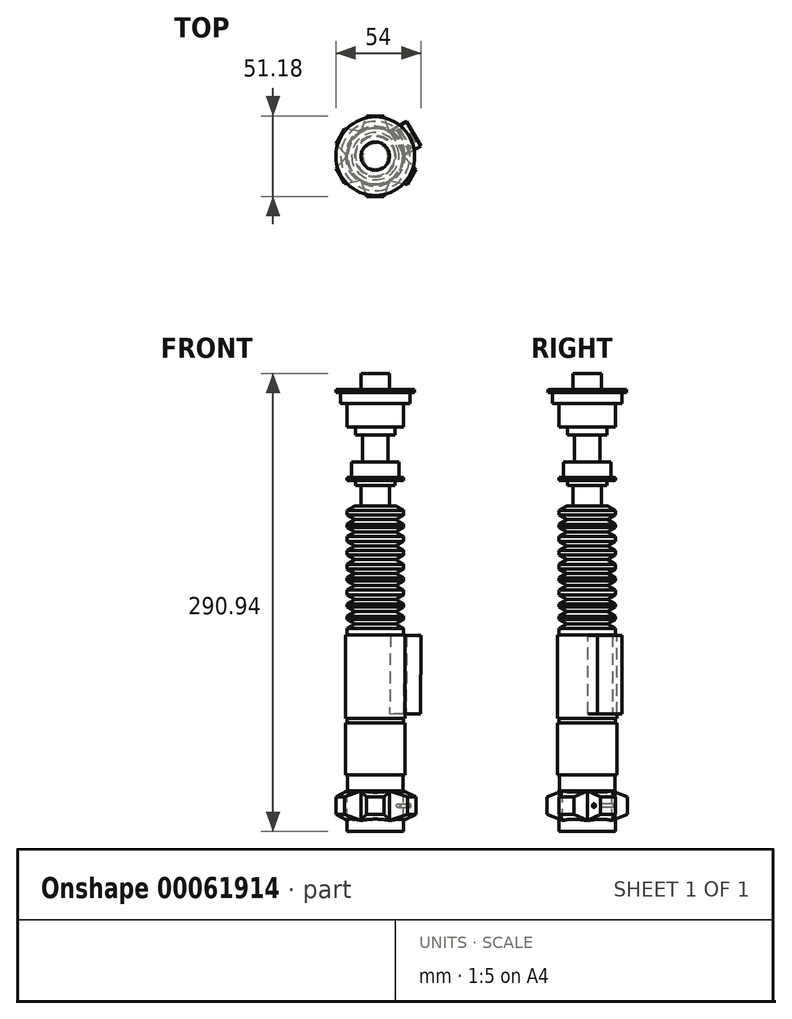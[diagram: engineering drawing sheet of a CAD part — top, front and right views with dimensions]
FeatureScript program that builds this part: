
annotation { "Feature Type Name" : "Feature", "Feature Type Description" : "" }
export const myFeature = defineFeature(function(context is Context, id is Id, definition is map)
    precondition{}
    {
        {
            var Q0;
            Q0=qCreatedBy(makeId("Front.planeOp"),FACE);
            var sketch = newSketch(context, id + "F0", { "sketchPlane" : qUnion([Q0])});
            skLineSegment(sketch, "E0.right", {"start": v(18, 0) * mm, "end": v(18, -10) * mm});
            skLineSegment(sketch, "E1", {"start": v(9, 0) * mm, "end": v(9, -95.13) * mm, "construction": true});
            skPoint(sketch, "E1.endSnap0", {"position": v(9, -10) * mm});
            skLineSegment(sketch, "E2.bottom", {"start": v(9, -10) * mm, "end": v(34, -10) * mm});
            skLineSegment(sketch, "E2.top", {"start": v(9, -12) * mm, "end": v(34, -12) * mm});
            skLineSegment(sketch, "E2.left", {"start": v(9, -10) * mm, "end": v(9, -12) * mm});
            skLineSegment(sketch, "E2.right", {"start": v(34, -10) * mm, "end": v(34, -12) * mm});
            skLineSegment(sketch, "E3.bottom", {"start": v(9, -12) * mm, "end": v(31, -12) * mm});
            skLineSegment(sketch, "E3.top", {"start": v(9, -19) * mm, "end": v(31, -19) * mm});
            skLineSegment(sketch, "E3.left", {"start": v(9, -12) * mm, "end": v(9, -19) * mm});
            skLineSegment(sketch, "E3.right", {"start": v(31, -12) * mm, "end": v(31, -19) * mm});
            skLineSegment(sketch, "E4.bottom", {"start": v(9, -19) * mm, "end": v(27, -19) * mm});
            skLineSegment(sketch, "E4.top", {"start": v(9, -34) * mm, "end": v(27, -34) * mm});
            skLineSegment(sketch, "E4.left", {"start": v(9, -19) * mm, "end": v(9, -34) * mm});
            skLineSegment(sketch, "E4.right", {"start": v(27, -19) * mm, "end": v(27, -34) * mm});
            skLineSegment(sketch, "E5.bottom", {"start": v(9, -34) * mm, "end": v(21.5, -34) * mm});
            skLineSegment(sketch, "E5.top", {"start": v(9, -39) * mm, "end": v(21.5, -39) * mm});
            skLineSegment(sketch, "E5.left", {"start": v(9, -34) * mm, "end": v(9, -39) * mm});
            skLineSegment(sketch, "E5.right", {"start": v(21.5, -34) * mm, "end": v(21.5, -39) * mm});
            skLineSegment(sketch, "E6.bottom", {"start": v(9, -39) * mm, "end": v(17, -39) * mm});
            skLineSegment(sketch, "E6.top", {"start": v(9, -56) * mm, "end": v(17, -56) * mm});
            skLineSegment(sketch, "E6.left", {"start": v(9, -39) * mm, "end": v(9, -56) * mm});
            skLineSegment(sketch, "E6.right", {"start": v(17, -39) * mm, "end": v(17, -56) * mm});
            skLineSegment(sketch, "E7.bottom", {"start": v(9, -56) * mm, "end": v(24, -56) * mm});
            skLineSegment(sketch, "E7.top", {"start": v(9, -66) * mm, "end": v(24, -66) * mm});
            skLineSegment(sketch, "E7.left", {"start": v(9, -56) * mm, "end": v(9, -66) * mm});
            skLineSegment(sketch, "E7.right", {"start": v(24, -56) * mm, "end": v(24, -66) * mm});
            skLineSegment(sketch, "E8.bottom", {"start": v(9, -66) * mm, "end": v(27, -66) * mm});
            skLineSegment(sketch, "E8.top", {"start": v(9, -68) * mm, "end": v(27, -68) * mm});
            skLineSegment(sketch, "E8.left", {"start": v(9, -66) * mm, "end": v(9, -68) * mm});
            skLineSegment(sketch, "E8.right", {"start": v(27, -66) * mm, "end": v(27, -68) * mm});
            skLineSegment(sketch, "E9.bottom", {"start": v(9, -68) * mm, "end": v(21.5, -68) * mm});
            skLineSegment(sketch, "E9.top", {"start": v(9, -71) * mm, "end": v(21.5, -71) * mm});
            skLineSegment(sketch, "E9.left", {"start": v(9, -68) * mm, "end": v(9, -71) * mm});
            skLineSegment(sketch, "E9.right", {"start": v(21.5, -68) * mm, "end": v(21.5, -71) * mm});
            skLineSegment(sketch, "E10.bottom", {"start": v(9, -71) * mm, "end": v(18, -71) * mm});
            skLineSegment(sketch, "E10.top", {"start": v(9, -84) * mm, "end": v(18, -84) * mm});
            skLineSegment(sketch, "E10.left", {"start": v(9, -71) * mm, "end": v(9, -84) * mm});
            skLineSegment(sketch, "E10.right", {"start": v(18, -71) * mm, "end": v(18, -84) * mm});
            skLineSegment(sketch, "E11", {"start": v(9, -84) * mm, "end": v(21.98, -84) * mm});
            skLineSegment(sketch, "E12.0", {"start": v(9, -86.9) * mm, "end": v(27, -86.9) * mm});
            skLineSegment(sketch, "E13", {"start": v(27, -86.9) * mm, "end": v(21.98, -84) * mm});
            skLineSegment(sketch, "E14.0", {"start": v(9, -89.9) * mm, "end": v(27, -89.9) * mm});
            skLineSegment(sketch, "E15", {"start": v(27, -86.9) * mm, "end": v(27, -89.9) * mm});
            skLineSegment(sketch, "E16", {"start": v(27, -89.9) * mm, "end": v(21.98, -92.8) * mm});
            skLineSegment(sketch, "E17.0", {"start": v(9, -92.8) * mm, "end": v(21.98, -92.8) * mm});
            skLineSegment(sketch, "E18.MirrorCS", {"start": v(27, -95.7) * mm, "end": v(21.98, -92.8) * mm});
            skLineSegment(sketch, "E19", {"start": v(27, -95.7) * mm, "end": v(9, -95.7) * mm});
            skLineSegment(sketch, "E20.0", {"start": v(27, -97.7) * mm, "end": v(9, -97.7) * mm});
            skLineSegment(sketch, "E21", {"start": v(27, -95.7) * mm, "end": v(27, -97.7) * mm});
            skLineSegment(sketch, "E22", {"start": v(27, -97.7) * mm, "end": v(21.98, -100.6) * mm});
            skLineSegment(sketch, "E23.0", {"start": v(21.98, -100.6) * mm, "end": v(9, -100.6) * mm});
            skLineSegment(sketch, "E24", {"start": v(21.98, -100.6) * mm, "end": v(27, -103.5) * mm});
            skLineSegment(sketch, "E25", {"start": v(27, -103.5) * mm, "end": v(9, -103.5) * mm});
            skLineSegment(sketch, "E26.0", {"start": v(27, -106.5) * mm, "end": v(9, -106.5) * mm});
            skLineSegment(sketch, "E27", {"start": v(27, -103.5) * mm, "end": v(27, -106.5) * mm});
            skLineSegment(sketch, "E28.MirrorCS", {"start": v(21.98, -109.4) * mm, "end": v(27, -106.5) * mm});
            skLineSegment(sketch, "E29.MirrorCS", {"start": v(21.98, -109.4) * mm, "end": v(9, -109.4) * mm});
            skLineSegment(sketch, "E30.MirrorCS", {"start": v(27, -112.3) * mm, "end": v(21.98, -109.4) * mm});
            skLineSegment(sketch, "E31.MirrorCS", {"start": v(27, -112.3) * mm, "end": v(9, -112.3) * mm});
            skLineSegment(sketch, "E32.MirrorCS", {"start": v(27, -115.3) * mm, "end": v(9, -115.3) * mm});
            skLineSegment(sketch, "E33.MirrorCS", {"start": v(21.98, -118.2) * mm, "end": v(27, -115.3) * mm});
            skLineSegment(sketch, "E34.MirrorCS", {"start": v(27, -121.1) * mm, "end": v(21.98, -118.2) * mm});
            skLineSegment(sketch, "E35.MirrorCS", {"start": v(21.98, -118.2) * mm, "end": v(9, -118.2) * mm});
            skLineSegment(sketch, "E36.MirrorCS", {"start": v(27, -121.1) * mm, "end": v(9, -121.1) * mm});
            skLineSegment(sketch, "E37.MirrorCS", {"start": v(27, -124.1) * mm, "end": v(9, -124.1) * mm});
            skLineSegment(sketch, "E38.MirrorCS", {"start": v(27, -124.1) * mm, "end": v(21.98, -127) * mm});
            skLineSegment(sketch, "E39.MirrorCS", {"start": v(21.98, -127) * mm, "end": v(9, -127) * mm});
            skLineSegment(sketch, "E40.MirrorCS", {"start": v(21.98, -127) * mm, "end": v(27, -129.9) * mm});
            skLineSegment(sketch, "E41.MirrorCS", {"start": v(27, -129.9) * mm, "end": v(9, -129.9) * mm});
            skLineSegment(sketch, "E42.MirrorCS", {"start": v(27, -129.74) * mm, "end": v(21.98, -126.84) * mm});
            skLineSegment(sketch, "E43.MirrorCS", {"start": v(27, -131.74) * mm, "end": v(9, -131.74) * mm});
            skLineSegment(sketch, "E44.MirrorCS", {"start": v(27, -131.74) * mm, "end": v(21.98, -134.64) * mm});
            skLineSegment(sketch, "E45.MirrorCS", {"start": v(9, -134.64) * mm, "end": v(21.98, -134.64) * mm});
            skLineSegment(sketch, "E46.MirrorCS", {"start": v(9, -137.54) * mm, "end": v(27, -137.54) * mm});
            skLineSegment(sketch, "E47.MirrorCS", {"start": v(9, -140.54) * mm, "end": v(27, -140.54) * mm});
            skLineSegment(sketch, "E48.MirrorCS", {"start": v(27, -140.54) * mm, "end": v(21.98, -143.44) * mm});
            skLineSegment(sketch, "E49", {"start": v(21.98, -134.64) * mm, "end": v(27, -137.54) * mm});
            skLineSegment(sketch, "E50", {"start": v(27, -140.54) * mm, "end": v(27, -137.54) * mm});
            skLineSegment(sketch, "E51", {"start": v(21.98, -143.44) * mm, "end": v(9, -143.44) * mm});
            skLineSegment(sketch, "E52.MirrorCS", {"start": v(27, -146.34) * mm, "end": v(21.98, -143.44) * mm});
            skLineSegment(sketch, "E53.MirrorCS", {"start": v(9, -146.34) * mm, "end": v(27, -146.34) * mm});
            skLineSegment(sketch, "E54", {"start": v(27, -131.74) * mm, "end": v(27, -129.74) * mm});
            skLineSegment(sketch, "E55", {"start": v(27, -124.1) * mm, "end": v(27, -121.1) * mm});
            skLineSegment(sketch, "E56.0", {"start": v(9, -148.34) * mm, "end": v(27, -148.34) * mm});
            skLineSegment(sketch, "E57", {"start": v(27, -148.34) * mm, "end": v(27, -146.34) * mm});
            skLineSegment(sketch, "E58.MirrorCS", {"start": v(27, -148.34) * mm, "end": v(21.98, -151.24) * mm});
            skLineSegment(sketch, "E59.MirrorCS", {"start": v(21.98, -151.24) * mm, "end": v(9, -151.24) * mm});
            skLineSegment(sketch, "E60.MirrorCS", {"start": v(27, -154.14) * mm, "end": v(21.98, -151.24) * mm});
            skLineSegment(sketch, "E61.MirrorCS", {"start": v(9, -154.14) * mm, "end": v(27, -154.14) * mm});
            skLineSegment(sketch, "E62.MirrorCS", {"start": v(9, -156.14) * mm, "end": v(27, -156.14) * mm});
            skLineSegment(sketch, "E63.MirrorCS", {"start": v(27, -154.14) * mm, "end": v(27, -156.14) * mm});
            skLineSegment(sketch, "E64.MirrorCS", {"start": v(27, -156.14) * mm, "end": v(21.98, -159.04) * mm});
            skLineSegment(sketch, "E65.MirrorCS", {"start": v(21.98, -159.04) * mm, "end": v(9, -159.04) * mm});
            skLineSegment(sketch, "E66.MirrorCS", {"start": v(27, -161.94) * mm, "end": v(21.98, -159.04) * mm});
            skLineSegment(sketch, "E67.MirrorCS", {"start": v(9, -161.94) * mm, "end": v(27, -161.94) * mm});
            skLineSegment(sketch, "E68", {"start": v(27, -161.94) * mm, "end": v(27, -165.94) * mm});
            skLineSegment(sketch, "E69", {"start": v(9, -165.94) * mm, "end": v(27, -165.94) * mm});
            skLineSegment(sketch, "E70", {"start": v(27, -112.3) * mm, "end": v(27, -115.3) * mm});
            skLineSegment(sketch, "E71", {"start": v(9, 0) * mm, "end": v(9, -165.94) * mm});
            skLineSegment(sketch, "E72", {"start": v(9, 0) * mm, "end": v(18, 0) * mm});
            skSolve(sketch);
        }
        {
            var Q0;
            {var subQ0=sQuery(id+"F0.wireOp",EDGE,"E39.MirrorCS");var subQ1=makeQuery(id+"F0.imprint","IMPRINT",EDGE,{"derivedFrom":subQ0});var subQ2=sQuery(id+"F0.wireOp",EDGE,"E40.MirrorCS");var subQ3=makeQuery(id+"F0.imprint","IMPRINT",EDGE,{"derivedFrom":subQ2});var subQ4=sQuery(id+"F0.wireOp",EDGE,"E41.MirrorCS");var subQ5=makeQuery(id+"F0.imprint","IMPRINT",EDGE,{"derivedFrom":subQ4});var subQ14=sQuery(id+"F0.wireOp",EDGE,"E37.MirrorCS");var subQ15=makeQuery(id+"F0.imprint","IMPRINT",EDGE,{"derivedFrom":subQ14});var subQ17=sQuery(id+"F0.wireOp",EDGE,"E65.MirrorCS");var subQ18=makeQuery(id+"F0.imprint","IMPRINT",EDGE,{"derivedFrom":subQ17});var subQ20=sQuery(id+"F0.wireOp",EDGE,"E67.MirrorCS");var subQ22=makeQuery(id+"F0.imprint","IMPRINT",EDGE,{"derivedFrom":subQ20});var subQ23=sQuery(id+"F0.wireOp",EDGE,"E62.MirrorCS");var subQ24=makeQuery(id+"F0.imprint","IMPRINT",EDGE,{"derivedFrom":subQ23});var subQ26=sQuery(id+"F0.wireOp",EDGE,"E61.MirrorCS");var subQ27=makeQuery(id+"F0.imprint","IMPRINT",EDGE,{"derivedFrom":subQ26});var subQ29=sQuery(id+"F0.wireOp",EDGE,"E59.MirrorCS");var subQ30=makeQuery(id+"F0.imprint","IMPRINT",EDGE,{"derivedFrom":subQ29});var subQ32=sQuery(id+"F0.wireOp",EDGE,"E56.0");var subQ33=makeQuery(id+"F0.imprint","IMPRINT",EDGE,{"derivedFrom":subQ32});var subQ35=sQuery(id+"F0.wireOp",EDGE,"E53.MirrorCS");var subQ36=makeQuery(id+"F0.imprint","IMPRINT",EDGE,{"derivedFrom":subQ35});var subQ38=sQuery(id+"F0.wireOp",EDGE,"E51");var subQ39=makeQuery(id+"F0.imprint","IMPRINT",EDGE,{"derivedFrom":subQ38});var subQ41=sQuery(id+"F0.wireOp",EDGE,"E47.MirrorCS");var subQ42=makeQuery(id+"F0.imprint","IMPRINT",EDGE,{"derivedFrom":subQ41});var subQ44=sQuery(id+"F0.wireOp",EDGE,"E46.MirrorCS");var subQ45=makeQuery(id+"F0.imprint","IMPRINT",EDGE,{"derivedFrom":subQ44});var subQ47=sQuery(id+"F0.wireOp",EDGE,"E45.MirrorCS");var subQ48=makeQuery(id+"F0.imprint","IMPRINT",EDGE,{"derivedFrom":subQ47});var subQ50=sQuery(id+"F0.wireOp",EDGE,"E43.MirrorCS");var subQ51=makeQuery(id+"F0.imprint","IMPRINT",EDGE,{"derivedFrom":subQ50});var subQ57=sQuery(id+"F0.wireOp",EDGE,"E36.MirrorCS");var subQ58=makeQuery(id+"F0.imprint","IMPRINT",EDGE,{"derivedFrom":subQ57});var subQ63=sQuery(id+"F0.wireOp",EDGE,"E32.MirrorCS");var subQ64=makeQuery(id+"F0.imprint","IMPRINT",EDGE,{"derivedFrom":subQ63});var subQ66=sQuery(id+"F0.wireOp",EDGE,"E31.MirrorCS");var subQ67=makeQuery(id+"F0.imprint","IMPRINT",EDGE,{"derivedFrom":subQ66});var subQ69=sQuery(id+"F0.wireOp",EDGE,"E29.MirrorCS");var subQ70=makeQuery(id+"F0.imprint","IMPRINT",EDGE,{"derivedFrom":subQ69});var subQ72=sQuery(id+"F0.wireOp",EDGE,"E26.0");var subQ73=makeQuery(id+"F0.imprint","IMPRINT",EDGE,{"derivedFrom":subQ72});var subQ75=sQuery(id+"F0.wireOp",EDGE,"E25");var subQ76=makeQuery(id+"F0.imprint","IMPRINT",EDGE,{"derivedFrom":subQ75});var subQ78=sQuery(id+"F0.wireOp",EDGE,"E23.0");var subQ79=makeQuery(id+"F0.imprint","IMPRINT",EDGE,{"derivedFrom":subQ78});var subQ81=sQuery(id+"F0.wireOp",EDGE,"E20.0");var subQ82=makeQuery(id+"F0.imprint","IMPRINT",EDGE,{"derivedFrom":subQ81});var subQ84=sQuery(id+"F0.wireOp",EDGE,"E19");var subQ85=makeQuery(id+"F0.imprint","IMPRINT",EDGE,{"derivedFrom":subQ84});var subQ87=sQuery(id+"F0.wireOp",EDGE,"E17.0");var subQ88=makeQuery(id+"F0.imprint","IMPRINT",EDGE,{"derivedFrom":subQ87});var subQ90=sQuery(id+"F0.wireOp",EDGE,"E14.0");var subQ91=makeQuery(id+"F0.imprint","IMPRINT",EDGE,{"derivedFrom":subQ90});var subQ93=sQuery(id+"F0.wireOp",EDGE,"E12.0");var subQ94=makeQuery(id+"F0.imprint","IMPRINT",EDGE,{"derivedFrom":subQ93});var subQ96=sQuery(id+"F0.wireOp",EDGE,"E10.top");var subQ97=makeQuery(id+"F0.imprint","IMPRINT",EDGE,{"derivedFrom":subQ96});var subQ99=sQuery(id+"F0.wireOp",EDGE,"E9.left");var subQ110=makeQuery(id+"F0.imprint","IMPRINT",EDGE,{"derivedFrom":sQuery(id+"F0.wireOp",EDGE,"E7.top")});var subQ111=makeQuery(id+"F0.imprint","IMPRINT",EDGE,{"derivedFrom":sQuery(id+"F0.wireOp",EDGE,"E6.top")});var subQ113=sQuery(id+"F0.wireOp",EDGE,"E5.left");var subQ119=sQuery(id+"F0.wireOp",EDGE,"E4.left");var subQ124=sQuery(id+"F0.wireOp",EDGE,"E3.left");var subQ129=sQuery(id+"F0.wireOp",EDGE,"E2.left");var subQ135=sQuery(id+"F0.wireOp",EDGE,"E0.right");Q0=qUnion([makeQuery(id+"F0.imprint","IMPRINT",FACE,{"disambiguationData":[TD([[makeQuery(id+"F0.imprint","IMPRINT",EDGE,{"derivedFrom":subQ135}),-1.0]])]}),makeQuery(id+"F0.imprint","IMPRINT",FACE,{"disambiguationData":[TD([[subQ22,-1.0]])]}),makeQuery(id+"F0.imprint","IMPRINT",FACE,{"disambiguationData":[TD([[makeQuery(id+"F0.imprint","IMPRINT",EDGE,{"derivedFrom":subQ129}),1.0]])]}),makeQuery(id+"F0.imprint","IMPRINT",FACE,{"disambiguationData":[TD([[makeQuery(id+"F0.imprint","IMPRINT",EDGE,{"derivedFrom":subQ124}),1.0]])]}),makeQuery(id+"F0.imprint","IMPRINT",FACE,{"disambiguationData":[TD([[makeQuery(id+"F0.imprint","IMPRINT",EDGE,{"derivedFrom":subQ119}),1.0]])]}),makeQuery(id+"F0.imprint","IMPRINT",FACE,{"disambiguationData":[TD([[makeQuery(id+"F0.imprint","IMPRINT",EDGE,{"derivedFrom":subQ113}),1.0]])]}),makeQuery(id+"F0.imprint","IMPRINT",FACE,{"disambiguationData":[TD([[subQ111,1.0]])]}),makeQuery(id+"F0.imprint","IMPRINT",FACE,{"disambiguationData":[TD([[subQ111,-1.0]])]}),makeQuery(id+"F0.imprint","IMPRINT",FACE,{"disambiguationData":[TD([[subQ110,-1.0]])]}),makeQuery(id+"F0.imprint","IMPRINT",FACE,{"disambiguationData":[TD([[makeQuery(id+"F0.imprint","IMPRINT",EDGE,{"derivedFrom":subQ99}),1.0]])]}),makeQuery(id+"F0.imprint","IMPRINT",FACE,{"disambiguationData":[TD([[subQ97,1.0]])]}),makeQuery(id+"F0.imprint","IMPRINT",FACE,{"disambiguationData":[TD([[subQ97,-1.0]])]}),makeQuery(id+"F0.imprint","IMPRINT",FACE,{"disambiguationData":[TD([[subQ94,-1.0]])]}),makeQuery(id+"F0.imprint","IMPRINT",FACE,{"disambiguationData":[TD([[subQ91,-1.0]])]}),makeQuery(id+"F0.imprint","IMPRINT",FACE,{"disambiguationData":[TD([[subQ88,-1.0]])]}),makeQuery(id+"F0.imprint","IMPRINT",FACE,{"disambiguationData":[TD([[subQ85,1.0]])]}),makeQuery(id+"F0.imprint","IMPRINT",FACE,{"disambiguationData":[TD([[subQ82,1.0]])]}),makeQuery(id+"F0.imprint","IMPRINT",FACE,{"disambiguationData":[TD([[subQ79,1.0]])]}),makeQuery(id+"F0.imprint","IMPRINT",FACE,{"disambiguationData":[TD([[subQ76,1.0]])]}),makeQuery(id+"F0.imprint","IMPRINT",FACE,{"disambiguationData":[TD([[subQ73,1.0]])]}),makeQuery(id+"F0.imprint","IMPRINT",FACE,{"disambiguationData":[TD([[subQ70,1.0]])]}),makeQuery(id+"F0.imprint","IMPRINT",FACE,{"disambiguationData":[TD([[subQ67,1.0]])]}),makeQuery(id+"F0.imprint","IMPRINT",FACE,{"disambiguationData":[TD([[subQ64,1.0]])]}),makeQuery(id+"F0.imprint","IMPRINT",FACE,{"disambiguationData":[TD([[makeQuery(id+"F0.imprint","IMPRINT",EDGE,{"derivedFrom":sQuery(id+"F0.wireOp",EDGE,"E34.MirrorCS")}),1.0]])]}),makeQuery(id+"F0.imprint","IMPRINT",FACE,{"disambiguationData":[TD([[subQ58,1.0]])]}),makeQuery(id+"F0.imprint","IMPRINT",FACE,{"disambiguationData":[TD([[subQ3,1.0]])]}),makeQuery(id+"F0.imprint","IMPRINT",FACE,{"disambiguationData":[TD([[subQ5,1.0]])]}),makeQuery(id+"F0.imprint","IMPRINT",FACE,{"disambiguationData":[TD([[subQ51,1.0]])]}),makeQuery(id+"F0.imprint","IMPRINT",FACE,{"disambiguationData":[TD([[subQ48,-1.0]])]}),makeQuery(id+"F0.imprint","IMPRINT",FACE,{"disambiguationData":[TD([[subQ45,-1.0]])]}),makeQuery(id+"F0.imprint","IMPRINT",FACE,{"disambiguationData":[TD([[subQ42,-1.0]])]}),makeQuery(id+"F0.imprint","IMPRINT",FACE,{"disambiguationData":[TD([[subQ39,1.0]])]}),makeQuery(id+"F0.imprint","IMPRINT",FACE,{"disambiguationData":[TD([[subQ36,-1.0]])]}),makeQuery(id+"F0.imprint","IMPRINT",FACE,{"disambiguationData":[TD([[subQ33,-1.0]])]}),makeQuery(id+"F0.imprint","IMPRINT",FACE,{"disambiguationData":[TD([[subQ30,1.0]])]}),makeQuery(id+"F0.imprint","IMPRINT",FACE,{"disambiguationData":[TD([[subQ27,-1.0]])]}),makeQuery(id+"F0.imprint","IMPRINT",FACE,{"disambiguationData":[TD([[subQ24,-1.0]])]}),makeQuery(id+"F0.imprint","IMPRINT",FACE,{"disambiguationData":[TD([[subQ18,1.0]])]}),makeQuery(id+"F0.imprint","IMPRINT",FACE,{"disambiguationData":[TD([[subQ15,1.0]])]}),makeQuery(id+"F0.imprint","IMPRINT",FACE,{"disambiguationData":[TD([[subQ1,1.0]])]})]);}
            var Q1;
            Q1=sQuery(id+"F0.wireOp",EDGE,"E71");
            revolve(context, id + "F1", {"entities" : qUnion([Q0]), "axis" : qUnion([Q1]), "revolveType" : RevolveType.FULL});
        }
        {
            var Q0;
            Q0=qCreatedBy(makeId("Front.planeOp"),FACE);
            var sketch = newSketch(context, id + "F2", { "sketchPlane" : qUnion([Q0])});
            skLineSegment(sketch, "E73.0", {"start": v(-9, -165.94) * mm, "end": v(27, -165.94) * mm});
            skLineSegment(sketch, "E74", {"start": v(9, -165.94) * mm, "end": v(9, -218.94) * mm});
            skLineSegment(sketch, "E75", {"start": v(9, -165.94) * mm, "end": v(28, -165.94) * mm});
            skLineSegment(sketch, "E76", {"start": v(28, -165.94) * mm, "end": v(28, -218.94) * mm});
            skLineSegment(sketch, "E77", {"start": v(28, -218.94) * mm, "end": v(9, -218.94) * mm});
            skLineSegment(sketch, "E78", {"start": v(9, -218.94) * mm, "end": v(9, -221.94) * mm});
            skLineSegment(sketch, "E79", {"start": v(9, -221.94) * mm, "end": v(27, -221.94) * mm});
            skLineSegment(sketch, "E80", {"start": v(27, -221.94) * mm, "end": v(27, -218.94) * mm});
            skLineSegment(sketch, "E81", {"start": v(9, -221.94) * mm, "end": v(9, -254.94) * mm});
            skLineSegment(sketch, "E82", {"start": v(9, -221.94) * mm, "end": v(28, -221.94) * mm});
            skLineSegment(sketch, "E83", {"start": v(28, -221.94) * mm, "end": v(28, -254.94) * mm});
            skLineSegment(sketch, "E84", {"start": v(28, -254.94) * mm, "end": v(9, -254.94) * mm});
            skLineSegment(sketch, "E85", {"start": v(9, -254.94) * mm, "end": v(9, -264.94) * mm});
            skLineSegment(sketch, "E86", {"start": v(9, -264.94) * mm, "end": v(26.5, -264.94) * mm});
            skLineSegment(sketch, "E87", {"start": v(26.5, -264.94) * mm, "end": v(26.5, -254.94) * mm});
            skSolve(sketch);
        }
        {
            var Q0;
            Q0 = qSketchRegion(id + "F2", true);
            var Q1;
            Q1=sQuery(id+"F2.wireOp",EDGE,"E74");
            revolve(context, id + "F3", {"operationType" : NewBodyOperationType.ADD, "entities" : qUnion([Q0]), "axis" : qUnion([Q1]), "revolveType" : RevolveType.FULL});
        }
        {
            var Q0;
            Q0=qCreatedBy(makeId("Front.planeOp"),FACE);
            var sketch = newSketch(context, id + "F4", { "sketchPlane" : qUnion([Q0])});
            skLineSegment(sketch, "E88.0", {"start": v(-8.5, -264.94) * mm, "end": v(26.5, -264.94) * mm});
            skLineSegment(sketch, "E89", {"start": v(9, -264.94) * mm, "end": v(9, -283.94) * mm});
            skLineSegment(sketch, "E90", {"start": v(9, -283.94) * mm, "end": v(27, -283.94) * mm});
            skLineSegment(sketch, "E91", {"start": v(27, -283.94) * mm, "end": v(27, -264.94) * mm});
            skLineSegment(sketch, "E92", {"start": v(27, -264.94) * mm, "end": v(9, -264.94) * mm});
            skLineSegment(sketch, "E93", {"start": v(9, -283.94) * mm, "end": v(9, -290.94) * mm});
            skLineSegment(sketch, "E94", {"start": v(9, -290.94) * mm, "end": v(27, -290.94) * mm});
            skLineSegment(sketch, "E95", {"start": v(27, -290.94) * mm, "end": v(27, -283.94) * mm});
            skSolve(sketch);
        }
        {
            var Q0;
            {var subQ0=sQuery(id+"F4.wireOp",EDGE,"E89");Q0=makeQuery(id+"F4.imprint","IMPRINT",FACE,{"disambiguationData":[TD([[makeQuery(id+"F4.imprint","IMPRINT",EDGE,{"derivedFrom":subQ0}),1.0]])]});}
            var Q1;
            Q1=sQuery(id+"F4.wireOp",EDGE,"E89");
            revolve(context, id + "F5", {"operationType" : NewBodyOperationType.ADD, "entities" : qUnion([Q0]), "axis" : qUnion([Q1]), "revolveType" : RevolveType.FULL});
        }
        {
            var Q0;
            Q0=makeQuery(id+"F5.opRevolve","SWEPT_FACE",FACE,{"disambiguationData":[OSD([sQuery(id+"F4.wireOp",EDGE,"E90")])]});
            var sketch = newSketch(context, id + "F6", { "sketchPlane" : qUnion([Q0])});
            skCircle(sketch, "E96.0", {"center": v(9, 0) * mm, "radius": 18 * mm, "construction": true});
            skLineSegment(sketch, "E97.0", {"start": v(0, -15.59) * mm, "end": v(-9, 0) * mm, "construction": true});
            skLineSegment(sketch, "E97.1", {"start": v(-9, 0) * mm, "end": v(0, 15.59) * mm, "construction": true});
            skLineSegment(sketch, "E97.2", {"start": v(0, 15.59) * mm, "end": v(18, 15.59) * mm, "construction": true});
            skLineSegment(sketch, "E97.3", {"start": v(18, 15.59) * mm, "end": v(27, 0) * mm, "construction": true});
            skLineSegment(sketch, "E97.4", {"start": v(27, 0) * mm, "end": v(18, -15.59) * mm, "construction": true});
            skLineSegment(sketch, "E97.5", {"start": v(18, -15.59) * mm, "end": v(0, -15.59) * mm, "construction": true});
            skSolve(sketch);
        }
        {
            var Q0;
            Q0=makeQuery(id+"F6.imprint","IMPRINT",FACE,{"disambiguationData":[TD([[makeQuery(id+"F6.imprint","IMPRINT",EDGE,{"derivedFrom":makeQuery(id+"F5.opRevolve","SWEPT_EDGE",EDGE,{"disambiguationData":[OSD([sQuery(id+"F4.wireOp",EDGE,"E90"),sQuery(id+"F4.wireOp",EDGE,"E91"),sQuery(id+"F4.wireOp",EDGE,"E95")])]})}),-1.0]])]});
            cPlane(context, id + "F7", {"entities" : qUnion([Q0]), "cplaneType" : CPlaneType.OFFSET, "offset" : 10 * mm, "width" : 150 * mm, "height" : 150 * mm});
        }
        {
            var Q0;
            Q0=qCreatedBy(id+"F7.planeOp",FACE);
            var sketch = newSketch(context, id + "F8", { "sketchPlane" : qUnion([Q0])});
            skLineSegment(sketch, "E98.0", {"start": v(18, 15.59) * mm, "end": v(27, 0) * mm, "construction": true});
            skLineSegment(sketch, "E98.1", {"start": v(27, 0) * mm, "end": v(18, -15.59) * mm, "construction": true});
            skLineSegment(sketch, "E98.2", {"start": v(18, -15.59) * mm, "end": v(0, -15.59) * mm, "construction": true});
            skLineSegment(sketch, "E98.3", {"start": v(0, -15.59) * mm, "end": v(-9, 0) * mm, "construction": true});
            skLineSegment(sketch, "E98.4", {"start": v(-9, 0) * mm, "end": v(0, 15.59) * mm, "construction": true});
            skLineSegment(sketch, "E98.5", {"start": v(0, 15.59) * mm, "end": v(18, 15.59) * mm, "construction": true});
            skSolve(sketch);
        }
        {
            var Q0;
            Q0=sQuery(id+"F6.wireOp",VERTEX,"E97.3.end");
            var Q1;
            Q1=sQuery(id+"F8.wireOp",VERTEX,"E98.1.start");
            var Q2;
            Q2=sQuery(id+"F6.wireOp",VERTEX,"E97.5.start");
            cPlane(context, id + "F9", {"entities" : qUnion([Q0, Q1, Q2]), "cplaneType" : CPlaneType.THREE_POINT, "offset" : 150 * mm, "width" : 150 * mm, "height" : 150 * mm});
        }
        {
            var Q0;
            Q0=qCreatedBy(id+"F9.planeOp",FACE);
            var sketch = newSketch(context, id + "F10", { "sketchPlane" : qUnion([Q0])});
            skLineSegment(sketch, "E99.0", {"start": v(13.5, -283.94) * mm, "end": v(-4.5, -283.94) * mm, "construction": true});
            skLineSegment(sketch, "E99.1", {"start": v(-13.5, -264.94) * mm, "end": v(22.5, -264.94) * mm, "construction": true});
            skLineSegment(sketch, "E100", {"start": v(13.5, -283.94) * mm, "end": v(-4.5, -283.94) * mm});
            skLineSegment(sketch, "E101", {"start": v(-4.5, -283.94) * mm, "end": v(-4.5, -264.94) * mm});
            skLineSegment(sketch, "E102", {"start": v(-4.5, -264.94) * mm, "end": v(13.5, -264.94) * mm, "construction": true});
            skLineSegment(sketch, "E103", {"start": v(13.5, -264.94) * mm, "end": v(13.5, -283.94) * mm});
            skLineSegment(sketch, "E104", {"start": v(13.5, -264.94) * mm, "end": v(-4.5, -264.94) * mm});
            skSolve(sketch);
        }
        {
            var Q0;
            Q0=qCreatedBy(id+"F9.planeOp",FACE);
            cPlane(context, id + "F11", {"entities" : qUnion([Q0]), "cplaneType" : CPlaneType.OFFSET, "offset" : 11 * mm, "oppositeDirection" : true, "width" : 150 * mm, "height" : 150 * mm});
        }
        {
            var Q0;
            Q0=qCreatedBy(id+"F11.planeOp",FACE);
            var sketch = newSketch(context, id + "F12", { "sketchPlane" : qUnion([Q0])});
            skLineSegment(sketch, "E105.0", {"start": v(13.5, -264.94) * mm, "end": v(13.5, -283.94) * mm, "construction": true});
            skLineSegment(sketch, "E105.1", {"start": v(13.5, -264.94) * mm, "end": v(-4.5, -264.94) * mm, "construction": true});
            skLineSegment(sketch, "E105.2", {"start": v(-4.5, -283.94) * mm, "end": v(-4.5, -264.94) * mm, "construction": true});
            skLineSegment(sketch, "E105.3", {"start": v(13.5, -283.94) * mm, "end": v(-4.5, -283.94) * mm, "construction": true});
            skLineSegment(sketch, "E106", {"start": v(4.5, -264.94) * mm, "end": v(4.5, -283.94) * mm, "construction": true});
            skLineSegment(sketch, "E107", {"start": v(13.5, -274.44) * mm, "end": v(-4.5, -274.44) * mm, "construction": true});
            skLineSegment(sketch, "E108", {"start": v(4.5, -268.94) * mm, "end": v(-1, -268.94) * mm});
            skLineSegment(sketch, "E109", {"start": v(-1, -268.94) * mm, "end": v(-1, -279.94) * mm});
            skLineSegment(sketch, "E110", {"start": v(-1, -279.94) * mm, "end": v(10, -279.94) * mm});
            skLineSegment(sketch, "E111", {"start": v(10, -279.94) * mm, "end": v(10, -268.94) * mm});
            skLineSegment(sketch, "E112", {"start": v(10, -268.94) * mm, "end": v(4.5, -268.94) * mm});
            skSolve(sketch);
        }
        {
            var Q1;
            Q1 = qSketchRegion(id + "F10", true);
            var Q2;
            Q2 = qSketchRegion(id + "F12", true);
            loft(context, id + "F13", {"operationType" : NewBodyOperationType.ADD, "sheetProfilesArray" : [{ "sheetProfileEntities" : qUnion([Q1]) }, { "sheetProfileEntities" : qUnion([Q2]) }]});
        }
        {
            var Q0;
            Q0=sQuery(id+"F8.wireOp",VERTEX,"E98.0.start");
            var Q1;
            Q1=sQuery(id+"F8.wireOp",VERTEX,"E98.1.start");
            var Q2;
            Q2=sQuery(id+"F6.wireOp",VERTEX,"E97.3.start");
            cPlane(context, id + "F14", {"entities" : qUnion([Q0, Q1, Q2]), "cplaneType" : CPlaneType.THREE_POINT, "offset" : 150 * mm, "width" : 150 * mm, "height" : 150 * mm});
        }
        {
            var Q0;
            Q0=qCreatedBy(id+"F14.planeOp",FACE);
            var sketch = newSketch(context, id + "F15", { "sketchPlane" : qUnion([Q0])});
            skLineSegment(sketch, "E113.0", {"start": v(4.5, -283.94) * mm, "end": v(-13.5, -283.94) * mm, "construction": true});
            skLineSegment(sketch, "E114.0", {"start": v(-22.5, -264.94) * mm, "end": v(13.5, -264.94) * mm, "construction": true});
            skLineSegment(sketch, "E115.bottom", {"start": v(4.5, -283.94) * mm, "end": v(-13.6, -283.94) * mm});
            skLineSegment(sketch, "E115.top", {"start": v(4.5, -264.94) * mm, "end": v(-13.6, -264.94) * mm});
            skLineSegment(sketch, "E115.left", {"start": v(4.5, -283.94) * mm, "end": v(4.5, -264.94) * mm});
            skLineSegment(sketch, "E115.right", {"start": v(-13.6, -283.94) * mm, "end": v(-13.6, -264.94) * mm});
            skSolve(sketch);
        }
        {
            var Q0;
            Q0=qCreatedBy(id+"F14.planeOp",FACE);
            cPlane(context, id + "F16", {"entities" : qUnion([Q0]), "cplaneType" : CPlaneType.OFFSET, "offset" : 11 * mm, "oppositeDirection" : true, "width" : 150 * mm, "height" : 150 * mm});
        }
        {
            var Q0;
            Q0=qCreatedBy(id+"F16.planeOp",FACE);
            var sketch = newSketch(context, id + "F17", { "sketchPlane" : qUnion([Q0])});
            skLineSegment(sketch, "E116.0", {"start": v(4.5, -283.94) * mm, "end": v(4.5, -264.94) * mm, "construction": true});
            skLineSegment(sketch, "E116.1", {"start": v(4.5, -283.94) * mm, "end": v(-13.6, -283.94) * mm, "construction": true});
            skLineSegment(sketch, "E116.2", {"start": v(-13.6, -283.94) * mm, "end": v(-13.6, -264.94) * mm, "construction": true});
            skLineSegment(sketch, "E116.3", {"start": v(4.5, -264.94) * mm, "end": v(-13.6, -264.94) * mm, "construction": true});
            skLineSegment(sketch, "E117", {"start": v(-4.55, -264.94) * mm, "end": v(-4.55, -283.94) * mm, "construction": true});
            skLineSegment(sketch, "E118", {"start": v(4.5, -274.44) * mm, "end": v(-13.6, -274.44) * mm, "construction": true});
            skLineSegment(sketch, "E119", {"start": v(-4.55, -268.94) * mm, "end": v(-10.05, -268.94) * mm});
            skLineSegment(sketch, "E120", {"start": v(-10.05, -268.94) * mm, "end": v(-10.05, -279.94) * mm});
            skLineSegment(sketch, "E121", {"start": v(-10.05, -279.94) * mm, "end": v(0.95, -279.94) * mm});
            skLineSegment(sketch, "E122", {"start": v(0.95, -279.94) * mm, "end": v(0.95, -268.94) * mm});
            skLineSegment(sketch, "E123", {"start": v(0.95, -268.94) * mm, "end": v(-4.55, -268.94) * mm});
            skSolve(sketch);
        }
        {
            var Q1;
            Q1 = qSketchRegion(id + "F15", true);
            var Q2;
            Q2 = qSketchRegion(id + "F17", true);
            loft(context, id + "F18", {"operationType" : NewBodyOperationType.ADD, "sheetProfilesArray" : [{ "sheetProfileEntities" : qUnion([Q1]) }, { "sheetProfileEntities" : qUnion([Q2]) }]});
        }
        {
            var Q0;
            Q0=sQuery(id+"F8.wireOp",VERTEX,"E98.0.start");
            var Q1;
            Q1=sQuery(id+"F8.wireOp",VERTEX,"E98.5.start");
            var Q2;
            Q2=sQuery(id+"F6.wireOp",VERTEX,"E97.3.start");
            cPlane(context, id + "F19", {"entities" : qUnion([Q0, Q1, Q2]), "cplaneType" : CPlaneType.THREE_POINT, "offset" : 150 * mm, "width" : 150 * mm, "height" : 150 * mm});
        }
        {
            var Q0;
            Q0=qCreatedBy(id+"F19.planeOp",FACE);
            var sketch = newSketch(context, id + "F20", { "sketchPlane" : qUnion([Q0])});
            skLineSegment(sketch, "E124.0", {"start": v(18, -283.94) * mm, "end": v(0, -283.94) * mm, "construction": true});
            skLineSegment(sketch, "E124.1", {"start": v(-9, -264.94) * mm, "end": v(18, -264.94) * mm, "construction": true});
            skLineSegment(sketch, "E125.bottom", {"start": v(0, -283.94) * mm, "end": v(18, -283.94) * mm});
            skLineSegment(sketch, "E125.top", {"start": v(0, -264.94) * mm, "end": v(18, -264.94) * mm});
            skLineSegment(sketch, "E125.left", {"start": v(0, -283.94) * mm, "end": v(0, -264.94) * mm});
            skLineSegment(sketch, "E125.right", {"start": v(18, -283.94) * mm, "end": v(18, -264.94) * mm});
            skSolve(sketch);
        }
        {
            var Q0;
            Q0=qCreatedBy(id+"F19.planeOp",FACE);
            cPlane(context, id + "F21", {"entities" : qUnion([Q0]), "cplaneType" : CPlaneType.OFFSET, "offset" : 10 * mm, "width" : 150 * mm, "height" : 150 * mm});
        }
        {
            var Q0;
            Q0=qCreatedBy(id+"F21.planeOp",FACE);
            var sketch = newSketch(context, id + "F22", { "sketchPlane" : qUnion([Q0])});
            skLineSegment(sketch, "E126.0", {"start": v(0, -264.94) * mm, "end": v(18, -264.94) * mm, "construction": true});
            skLineSegment(sketch, "E126.1", {"start": v(0, -283.94) * mm, "end": v(0, -264.94) * mm, "construction": true});
            skLineSegment(sketch, "E126.2", {"start": v(0, -283.94) * mm, "end": v(18, -283.94) * mm, "construction": true});
            skLineSegment(sketch, "E126.3", {"start": v(18, -283.94) * mm, "end": v(18, -264.94) * mm, "construction": true});
            skLineSegment(sketch, "E127", {"start": v(9, -264.94) * mm, "end": v(9, -283.94) * mm, "construction": true});
            skLineSegment(sketch, "E128", {"start": v(0, -274.44) * mm, "end": v(18, -274.44) * mm, "construction": true});
            skLineSegment(sketch, "E129", {"start": v(3.5, -268.94) * mm, "end": v(14.5, -268.94) * mm});
            skLineSegment(sketch, "E130", {"start": v(14.5, -268.94) * mm, "end": v(14.5, -279.94) * mm});
            skLineSegment(sketch, "E131", {"start": v(14.5, -279.94) * mm, "end": v(3.5, -279.94) * mm});
            skLineSegment(sketch, "E132", {"start": v(3.5, -279.94) * mm, "end": v(3.5, -268.94) * mm});
            skSolve(sketch);
        }
        {
            var Q1;
            Q1 = qSketchRegion(id + "F20", true);
            var Q2;
            Q2 = qSketchRegion(id + "F22", true);
            loft(context, id + "F23", {"operationType" : NewBodyOperationType.ADD, "sheetProfilesArray" : [{ "sheetProfileEntities" : qUnion([Q1]) }, { "sheetProfileEntities" : qUnion([Q2]) }]});
        }
        {
            var Q0;
            Q0=sQuery(id+"F8.wireOp",VERTEX,"E98.4.start");
            var Q1;
            Q1=sQuery(id+"F8.wireOp",VERTEX,"E98.5.start");
            var Q2;
            Q2=sQuery(id+"F6.wireOp",VERTEX,"E97.2.start");
            cPlane(context, id + "F24", {"entities" : qUnion([Q0, Q1, Q2]), "cplaneType" : CPlaneType.THREE_POINT, "offset" : 150 * mm, "width" : 150 * mm, "height" : 150 * mm});
        }
        {
            var Q0;
            Q0=qCreatedBy(id+"F24.planeOp",FACE);
            var sketch = newSketch(context, id + "F25", { "sketchPlane" : qUnion([Q0])});
            skLineSegment(sketch, "E133.0", {"start": v(-13.5, -283.94) * mm, "end": v(4.5, -283.94) * mm, "construction": true});
            skLineSegment(sketch, "E133.1", {"start": v(-13.5, -264.94) * mm, "end": v(13.5, -264.94) * mm, "construction": true});
            skLineSegment(sketch, "E134.bottom", {"start": v(4.5, -283.94) * mm, "end": v(-13.5, -283.94) * mm});
            skLineSegment(sketch, "E134.top", {"start": v(4.5, -264.94) * mm, "end": v(-13.5, -264.94) * mm});
            skLineSegment(sketch, "E134.left", {"start": v(4.5, -283.94) * mm, "end": v(4.5, -264.94) * mm});
            skLineSegment(sketch, "E134.right", {"start": v(-13.5, -283.94) * mm, "end": v(-13.5, -264.94) * mm});
            skSolve(sketch);
        }
        {
            var Q0;
            Q0=qCreatedBy(id+"F24.planeOp",FACE);
            cPlane(context, id + "F26", {"entities" : qUnion([Q0]), "cplaneType" : CPlaneType.OFFSET, "offset" : 10 * mm, "oppositeDirection" : true, "width" : 150 * mm, "height" : 150 * mm});
        }
        {
            var Q0;
            Q0=qCreatedBy(id+"F26.planeOp",FACE);
            var sketch = newSketch(context, id + "F27", { "sketchPlane" : qUnion([Q0])});
            skLineSegment(sketch, "E135.0", {"start": v(4.5, -264.94) * mm, "end": v(-13.5, -264.94) * mm, "construction": true});
            skLineSegment(sketch, "E135.1", {"start": v(4.5, -283.94) * mm, "end": v(4.5, -264.94) * mm, "construction": true});
            skLineSegment(sketch, "E135.2", {"start": v(4.5, -283.94) * mm, "end": v(-13.5, -283.94) * mm, "construction": true});
            skLineSegment(sketch, "E135.3", {"start": v(-13.5, -283.94) * mm, "end": v(-13.5, -264.94) * mm, "construction": true});
            skLineSegment(sketch, "E136", {"start": v(-4.5, -264.94) * mm, "end": v(-4.5, -283.94) * mm, "construction": true});
            skLineSegment(sketch, "E137", {"start": v(4.5, -274.44) * mm, "end": v(-13.5, -274.44) * mm, "construction": true});
            skLineSegment(sketch, "E138", {"start": v(1, -268.94) * mm, "end": v(-10, -268.94) * mm});
            skLineSegment(sketch, "E139", {"start": v(-10, -268.94) * mm, "end": v(-10, -279.94) * mm});
            skLineSegment(sketch, "E140", {"start": v(1, -268.94) * mm, "end": v(1, -279.94) * mm});
            skLineSegment(sketch, "E141", {"start": v(1, -279.94) * mm, "end": v(-10, -279.94) * mm});
            skSolve(sketch);
        }
        {
            var Q1;
            Q1 = qSketchRegion(id + "F25", true);
            var Q2;
            Q2 = qSketchRegion(id + "F27", true);
            loft(context, id + "F28", {"operationType" : NewBodyOperationType.ADD, "sheetProfilesArray" : [{ "sheetProfileEntities" : qUnion([Q1]) }, { "sheetProfileEntities" : qUnion([Q2]) }]});
        }
        {
            var Q0;
            Q0=sQuery(id+"F8.wireOp",VERTEX,"E98.3.start");
            var Q1;
            Q1=sQuery(id+"F8.wireOp",VERTEX,"E98.4.start");
            var Q2;
            Q2=sQuery(id+"F6.wireOp",VERTEX,"E97.1.start");
            cPlane(context, id + "F29", {"entities" : qUnion([Q0, Q1, Q2]), "cplaneType" : CPlaneType.THREE_POINT, "offset" : 150 * mm, "width" : 150 * mm, "height" : 150 * mm});
        }
        {
            var Q0;
            Q0=qCreatedBy(id+"F29.planeOp",FACE);
            var sketch = newSketch(context, id + "F30", { "sketchPlane" : qUnion([Q0])});
            skLineSegment(sketch, "E142.0", {"start": v(-4.5, -283.94) * mm, "end": v(13.5, -283.94) * mm, "construction": true});
            skLineSegment(sketch, "E142.1", {"start": v(22.5, -264.94) * mm, "end": v(-4.5, -264.94) * mm, "construction": true});
            skLineSegment(sketch, "E143.bottom", {"start": v(13.5, -283.94) * mm, "end": v(-4.5, -283.94) * mm});
            skLineSegment(sketch, "E143.top", {"start": v(13.5, -264.94) * mm, "end": v(-4.5, -264.94) * mm});
            skLineSegment(sketch, "E143.left", {"start": v(13.5, -283.94) * mm, "end": v(13.5, -264.94) * mm});
            skLineSegment(sketch, "E143.right", {"start": v(-4.5, -283.94) * mm, "end": v(-4.5, -264.94) * mm});
            skSolve(sketch);
        }
        {
            var Q0;
            Q0=qCreatedBy(id+"F29.planeOp",FACE);
            cPlane(context, id + "F31", {"entities" : qUnion([Q0]), "cplaneType" : CPlaneType.OFFSET, "offset" : 10 * mm, "oppositeDirection" : true, "width" : 150 * mm, "height" : 150 * mm});
        }
        {
            var Q0;
            Q0=qCreatedBy(id+"F31.planeOp",FACE);
            var sketch = newSketch(context, id + "F32", { "sketchPlane" : qUnion([Q0])});
            skLineSegment(sketch, "E144.0", {"start": v(13.5, -264.94) * mm, "end": v(-4.5, -264.94) * mm, "construction": true});
            skLineSegment(sketch, "E144.1", {"start": v(13.5, -283.94) * mm, "end": v(13.5, -264.94) * mm, "construction": true});
            skLineSegment(sketch, "E144.2", {"start": v(13.5, -283.94) * mm, "end": v(-4.5, -283.94) * mm, "construction": true});
            skLineSegment(sketch, "E144.3", {"start": v(-4.5, -283.94) * mm, "end": v(-4.5, -264.94) * mm, "construction": true});
            skLineSegment(sketch, "E145", {"start": v(4.5, -264.94) * mm, "end": v(4.5, -283.94) * mm, "construction": true});
            skLineSegment(sketch, "E146", {"start": v(13.5, -274.44) * mm, "end": v(-4.5, -274.44) * mm, "construction": true});
            skLineSegment(sketch, "E147", {"start": v(10, -268.94) * mm, "end": v(-1, -268.94) * mm});
            skLineSegment(sketch, "E148", {"start": v(-1, -268.94) * mm, "end": v(-1, -279.94) * mm});
            skLineSegment(sketch, "E149", {"start": v(-1, -279.94) * mm, "end": v(10, -279.94) * mm});
            skLineSegment(sketch, "E150", {"start": v(10, -279.94) * mm, "end": v(10, -268.94) * mm});
            skSolve(sketch);
        }
        {
            var Q1;
            Q1 = qSketchRegion(id + "F30", true);
            var Q2;
            Q2 = qSketchRegion(id + "F32", true);
            loft(context, id + "F33", {"operationType" : NewBodyOperationType.ADD, "sheetProfilesArray" : [{ "sheetProfileEntities" : qUnion([Q1]) }, { "sheetProfileEntities" : qUnion([Q2]) }]});
        }
        {
            var Q0;
            Q0=sQuery(id+"F8.wireOp",VERTEX,"E98.3.start");
            var Q1;
            Q1=sQuery(id+"F8.wireOp",VERTEX,"E98.2.start");
            var Q2;
            Q2=sQuery(id+"F6.wireOp",VERTEX,"E97.0.start");
            cPlane(context, id + "F34", {"entities" : qUnion([Q0, Q1, Q2]), "cplaneType" : CPlaneType.THREE_POINT, "offset" : 150 * mm, "width" : 150 * mm, "height" : 150 * mm});
        }
        {
            var Q0;
            Q0=qCreatedBy(id+"F34.planeOp",FACE);
            var sketch = newSketch(context, id + "F35", { "sketchPlane" : qUnion([Q0])});
            skLineSegment(sketch, "E151.0", {"start": v(-18, -283.94) * mm, "end": v(0, -283.94) * mm, "construction": true});
            skLineSegment(sketch, "E151.1", {"start": v(-18, -264.94) * mm, "end": v(0, -264.94) * mm, "construction": true});
            skLineSegment(sketch, "E152.bottom", {"start": v(-18, -283.94) * mm, "end": v(0, -283.94) * mm});
            skLineSegment(sketch, "E152.top", {"start": v(-18, -264.94) * mm, "end": v(0, -264.94) * mm});
            skLineSegment(sketch, "E152.left", {"start": v(-18, -283.94) * mm, "end": v(-18, -264.94) * mm});
            skLineSegment(sketch, "E152.right", {"start": v(0, -283.94) * mm, "end": v(0, -264.94) * mm});
            skSolve(sketch);
        }
        {
            var Q0;
            Q0=qCreatedBy(id+"F34.planeOp",FACE);
            cPlane(context, id + "F36", {"entities" : qUnion([Q0]), "cplaneType" : CPlaneType.OFFSET, "offset" : 10 * mm, "width" : 150 * mm, "height" : 150 * mm});
        }
        {
            var Q0;
            Q0=qCreatedBy(id+"F36.planeOp",FACE);
            var sketch = newSketch(context, id + "F37", { "sketchPlane" : qUnion([Q0])});
            skLineSegment(sketch, "E153.0", {"start": v(-18, -264.94) * mm, "end": v(0, -264.94) * mm, "construction": true});
            skLineSegment(sketch, "E153.1", {"start": v(-18, -283.94) * mm, "end": v(-18, -264.94) * mm, "construction": true});
            skLineSegment(sketch, "E153.2", {"start": v(-18, -283.94) * mm, "end": v(0, -283.94) * mm, "construction": true});
            skLineSegment(sketch, "E153.3", {"start": v(0, -283.94) * mm, "end": v(0, -264.94) * mm, "construction": true});
            skLineSegment(sketch, "E154", {"start": v(-9, -264.94) * mm, "end": v(-9, -283.94) * mm, "construction": true});
            skLineSegment(sketch, "E155", {"start": v(-18, -274.44) * mm, "end": v(0, -274.44) * mm, "construction": true});
            skLineSegment(sketch, "E156.bottom", {"start": v(-14.5, -268.94) * mm, "end": v(-3.5, -268.94) * mm});
            skLineSegment(sketch, "E156.top", {"start": v(-14.5, -279.94) * mm, "end": v(-3.5, -279.94) * mm});
            skLineSegment(sketch, "E156.left", {"start": v(-14.5, -268.94) * mm, "end": v(-14.5, -279.94) * mm});
            skLineSegment(sketch, "E156.right", {"start": v(-3.5, -268.94) * mm, "end": v(-3.5, -279.94) * mm});
            skSolve(sketch);
        }
        {
            var Q1;
            Q1 = qSketchRegion(id + "F35", true);
            var Q2;
            Q2 = qSketchRegion(id + "F37", true);
            loft(context, id + "F38", {"operationType" : NewBodyOperationType.ADD, "sheetProfilesArray" : [{ "sheetProfileEntities" : qUnion([Q1]) }, { "sheetProfileEntities" : qUnion([Q2]) }]});
        }
        {
            var Q0;
            Q0=makeQuery(id+"F13.opLoft","CAP_FACE",FACE,{"disambiguationData":[OSD([makeQuery(id+"F12.imprint","IMPRINT",FACE,{"disambiguationData":[TD([[makeQuery(id+"F12.imprint","IMPRINT",EDGE,{"derivedFrom":sQuery(id+"F12.wireOp",EDGE,"E108")}),1.0]])]})])],"isStart":true});
            var sketch = newSketch(context, id + "F39", { "sketchPlane" : qUnion([Q0])});
            skLineSegment(sketch, "E157.0", {"start": v(-13.47, -283.9) * mm, "end": v(-13.47, -264.97) * mm, "construction": true});
            skLineSegment(sketch, "E158.0", {"start": v(-10, -268.94) * mm, "end": v(-10, -279.94) * mm, "construction": true});
            skSolve(sketch);
        }
        {
            var Q0;
            {var subQ0=sQuery(id+"F12.wireOp",EDGE,"E112");var subQ1=sQuery(id+"F12.wireOp",EDGE,"E111");var subQ2=sQuery(id+"F10.wireOp",EDGE,"E104");var subQ3=sQuery(id+"F10.wireOp",EDGE,"E103");Q0=makeQuery(id+"F18.boolean.opBoolean","INTERSECT",VERTEX,{"derivedFrom":[makeQuery(id+"F13.opLoft","SWEPT_FACE",FACE,{"disambiguationData":[OSD([sQuery(id+"F10.wireOp",EDGE,"E100"),subQ3,subQ2,sQuery(id+"F12.wireOp",EDGE,"E110"),subQ1,subQ0])]}),makeQuery(id+"F13.opLoft","SWEPT_FACE",FACE,{"disambiguationData":[OSD([sQuery(id+"F10.wireOp",EDGE,"E101"),subQ3,subQ2,sQuery(id+"F12.wireOp",EDGE,"E108"),sQuery(id+"F12.wireOp",EDGE,"E109"),subQ1,subQ0])]}),makeQuery(id+"F18.opLoft","SWEPT_FACE",FACE,{"disambiguationData":[OSD([sQuery(id+"F15.wireOp",EDGE,"E115.bottom"),sQuery(id+"F15.wireOp",EDGE,"E115.top"),sQuery(id+"F15.wireOp",EDGE,"E115.right"),sQuery(id+"F17.wireOp",EDGE,"E119"),sQuery(id+"F17.wireOp",EDGE,"E120"),sQuery(id+"F17.wireOp",EDGE,"E121")])]})]});}
            var Q1;
            Q1=sQuery(id+"F39.wireOp",VERTEX,"E157.0.end");
            var Q2;
            Q2=sQuery(id+"F39.wireOp",VERTEX,"E157.0.start");
            cPlane(context, id + "F40", {"entities" : qUnion([Q0, Q1, Q2]), "cplaneType" : CPlaneType.THREE_POINT, "offset" : 150 * mm, "width" : 150 * mm, "height" : 150 * mm});
        }
        {
            var Q0;
            Q0=qCreatedBy(id+"F40.planeOp",FACE);
            var sketch = newSketch(context, id + "F41", { "sketchPlane" : qUnion([Q0])});
            skLineSegment(sketch, "E159.0", {"start": v(34.38, -268.94) * mm, "end": v(34.38, -279.94) * mm, "construction": true});
            skLineSegment(sketch, "E160", {"start": v(34.38, -268.94) * mm, "end": v(23.43, -268.94) * mm, "construction": true});
            skLineSegment(sketch, "E161", {"start": v(23.43, -268.94) * mm, "end": v(23.43, -279.94) * mm, "construction": true});
            skLineSegment(sketch, "E162", {"start": v(23.43, -279.94) * mm, "end": v(34.38, -279.94) * mm, "construction": true});
            skLineSegment(sketch, "E163", {"start": v(23.43, -268.94) * mm, "end": v(34.38, -279.94) * mm, "construction": true});
            skCircle(sketch, "E164", {"center": v(28.9, -274.44) * mm, "radius": 1.2 * mm});
            skSolve(sketch);
        }
        {
            var Q0;
            Q0=makeQuery(id+"F41.imprint","IMPRINT",FACE,{"disambiguationData":[TD([[makeQuery(id+"F41.imprint","IMPRINT",EDGE,{"derivedFrom":sQuery(id+"F41.wireOp",EDGE,"E164")}),1.0]])]});
            extrude(context, id + "F42", {"entities" : qUnion([Q0]), "operationType" : NewBodyOperationType.REMOVE, "endBound" : BoundingType.THROUGH_ALL, "oppositeDirection" : true, "depth" : 25 * mm});
        }
        {
            var Q0;
            Q0=makeQuery(id+"F4.imprint","IMPRINT",FACE,{"disambiguationData":[TD([[makeQuery(id+"F4.imprint","IMPRINT",EDGE,{"derivedFrom":sQuery(id+"F4.wireOp",EDGE,"E90")}),-1.0]])]});
            var Q1;
            Q1=sQuery(id+"F4.wireOp",EDGE,"E93");
            revolve(context, id + "F43", {"operationType" : NewBodyOperationType.ADD, "entities" : qUnion([Q0]), "axis" : qUnion([Q1]), "revolveType" : RevolveType.FULL});
        }
        {
            var Q0;
            Q0=qCreatedBy(makeId("Top.planeOp"),FACE);
            var sketch = newSketch(context, id + "F44", { "sketchPlane" : qUnion([Q0])});
            skCircle(sketch, "E165.0", {"center": v(9, 0) * mm, "radius": 17.5 * mm, "construction": true});
            skLineSegment(sketch, "E166.0", {"start": v(29.28, 18.06) * mm, "end": v(34.78, 8.53) * mm, "construction": true});
            skLineSegment(sketch, "E167", {"start": v(32.03, 13.3) * mm, "end": v(24.16, 8.75) * mm, "construction": true});
            skSolve(sketch);
        }
        {
            var Q0;
            Q0=makeQuery(id+"F18.opLoft","MID_CAP_VERTEX",VERTEX,{"disambiguationData":[OSD([sQuery(id+"F15.wireOp",EDGE,"E115.top"),sQuery(id+"F15.wireOp",EDGE,"E115.right")])],"capPos":0.0});
            var Q1;
            Q1=makeQuery(id+"F38.boolean.opBoolean","MERGE",VERTEX,{"derivedFrom":[makeQuery(id+"F13.opLoft","MID_CAP_VERTEX",VERTEX,{"disambiguationData":[OSD([sQuery(id+"F10.wireOp",EDGE,"E101"),sQuery(id+"F10.wireOp",EDGE,"E104")])],"capPos":0.0}),makeQuery(id+"F38.opLoft","MID_CAP_VERTEX",VERTEX,{"disambiguationData":[OSD([sQuery(id+"F35.wireOp",EDGE,"E152.top"),sQuery(id+"F35.wireOp",EDGE,"E152.left")])],"capPos":0.0})]});
            var Q2;
            Q2=sQuery(id+"F44.wireOp",VERTEX,"E167.end");
            cPlane(context, id + "F45", {"entities" : qUnion([Q0, Q1, Q2]), "cplaneType" : CPlaneType.THREE_POINT, "offset" : 150 * mm, "width" : 150 * mm, "height" : 150 * mm});
        }
        {
            var Q0;
            Q0=qCreatedBy(id+"F45.planeOp",FACE);
            var sketch = newSketch(context, id + "F46", { "sketchPlane" : qUnion([Q0])});
            skEllipse(sketch, "E168.0", {"center": v(5.22, -165.86) * mm, "majorRadius": 19 * mm, "minorRadius": 0.13 * mm, "majorAxis": v(1, 0), "construction": true});
            skLineSegment(sketch, "E169", {"start": v(5.22, -165.86) * mm, "end": v(5.22, -215.86) * mm, "construction": true});
            skLineSegment(sketch, "E170", {"start": v(5.22, -215.86) * mm, "end": v(14.22, -215.86) * mm});
            skLineSegment(sketch, "E171", {"start": v(14.22, -215.86) * mm, "end": v(14.22, -165.94) * mm});
            skLineSegment(sketch, "E172", {"start": v(14.22, -165.94) * mm, "end": v(5.22, -165.86) * mm});
            skLineSegment(sketch, "E173", {"start": v(-3.78, -166.02) * mm, "end": v(-3.78, -215.86) * mm});
            skLineSegment(sketch, "E174", {"start": v(-3.78, -215.86) * mm, "end": v(14.22, -215.86) * mm});
            skLineSegment(sketch, "E175", {"start": v(14.22, -165.94) * mm, "end": v(-3.78, -166.02) * mm});
            skSolve(sketch);
        }
        {
            var Q0;
            Q0 = qSketchRegion(id + "F46", true);
            extrude(context, id + "F47", {"entities" : qUnion([Q0]), "oppositeDirection" : true, "depth" : 12 * mm});
        }
    });
